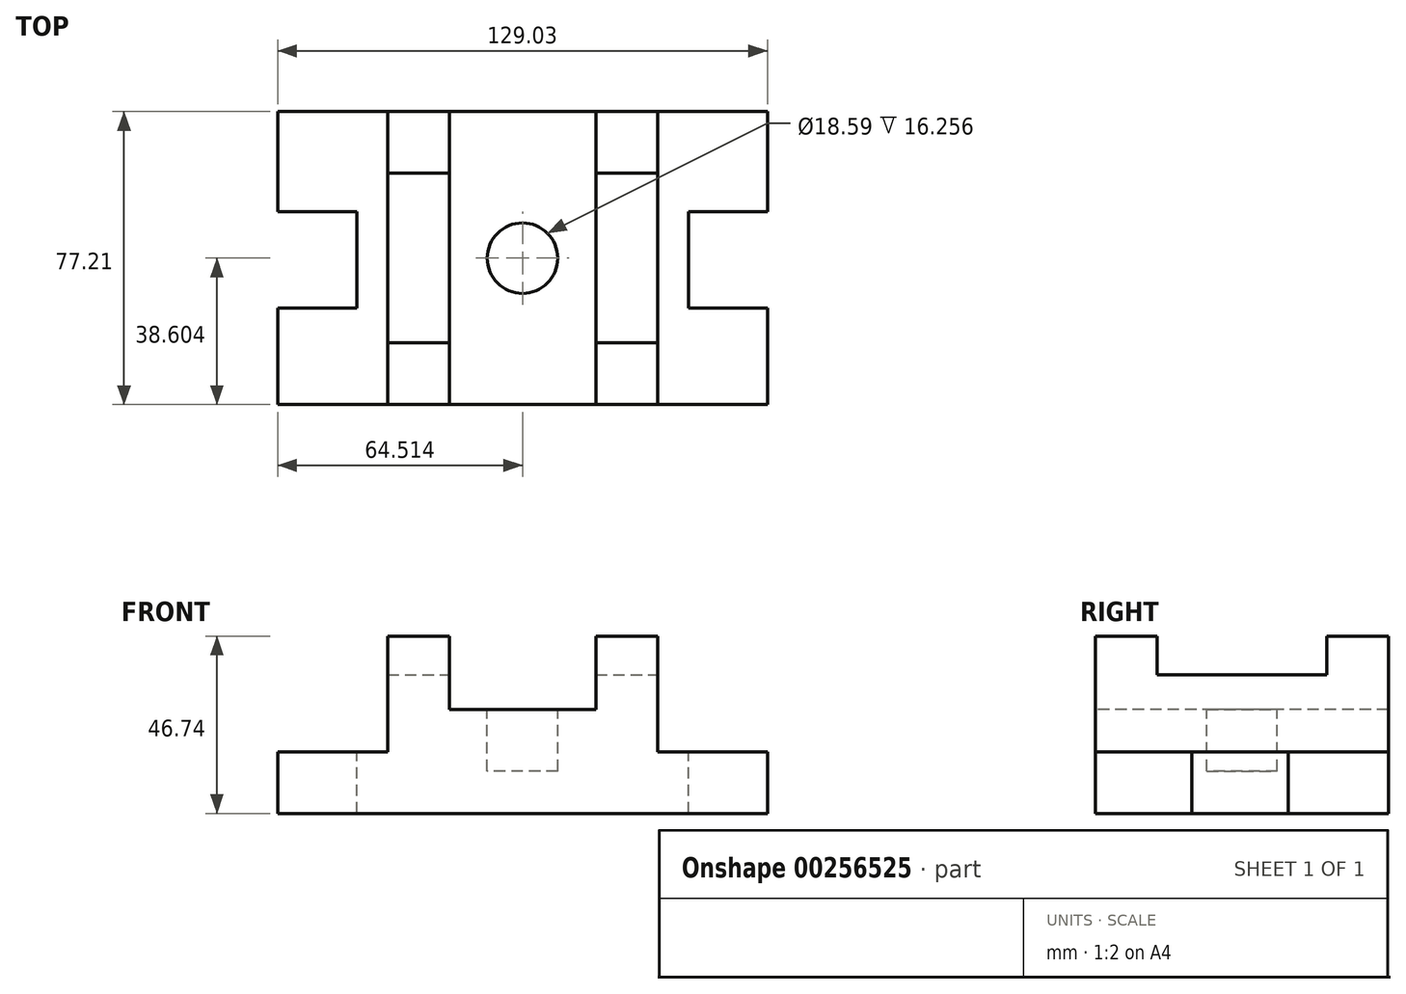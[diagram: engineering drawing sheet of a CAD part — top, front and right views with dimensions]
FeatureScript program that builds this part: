
annotation { "Feature Type Name" : "Feature", "Feature Type Description" : "" }
export const myFeature = defineFeature(function(context is Context, id is Id, definition is map)
    precondition{}
    {
        {
            var Q0;
            Q0=qCreatedBy(makeId("Top.planeOp"),FACE);
            var sketch = newSketch(context, id + "F0", { "sketchPlane" : qUnion([Q0])});
            skLineSegment(sketch, "E0.bottom", {"start": v(-63.44, 39.07) * mm, "end": v(65.59, 39.07) * mm});
            skLineSegment(sketch, "E0.top", {"start": v(-63.44, -38.14) * mm, "end": v(65.59, -38.14) * mm});
            skLineSegment(sketch, "E0.left", {"start": v(-63.44, 39.07) * mm, "end": v(-63.44, -38.14) * mm});
            skLineSegment(sketch, "E0.right", {"start": v(65.59, 39.07) * mm, "end": v(65.59, -38.14) * mm});
            skSolve(sketch);
        }
        {
            var Q0;
            Q0 = qSketchRegion(id + "F0", true);
            extrude(context, id + "F1", {"entities" : qUnion([Q0]), "depth" : 46.74 * mm});
        }
        {
            var Q0;
            Q0=makeQuery(id+"F1.opExtrude","CAP_FACE",FACE,{"disambiguationData":[OSD([sQuery(id+"F0.wireOp",EDGE,"E0.bottom"),sQuery(id+"F0.wireOp",EDGE,"E0.top"),sQuery(id+"F0.wireOp",EDGE,"E0.left"),sQuery(id+"F0.wireOp",EDGE,"E0.right")])],"isStart":false});
            var sketch = newSketch(context, id + "F2", { "sketchPlane" : qUnion([Q0])});
            skLineSegment(sketch, "E1.bottom", {"start": v(-63.44, 39.07) * mm, "end": v(-34.49, 39.07) * mm});
            skLineSegment(sketch, "E1.top", {"start": v(-63.44, -38.14) * mm, "end": v(-34.49, -38.14) * mm});
            skLineSegment(sketch, "E1.left", {"start": v(-63.44, 39.07) * mm, "end": v(-63.44, -38.14) * mm});
            skLineSegment(sketch, "E1.right", {"start": v(-34.49, 39.07) * mm, "end": v(-34.49, -38.14) * mm});
            skLineSegment(sketch, "E2.bottom", {"start": v(65.59, 39.07) * mm, "end": v(36.63, 39.07) * mm});
            skLineSegment(sketch, "E2.top", {"start": v(65.59, -38.14) * mm, "end": v(36.63, -38.14) * mm});
            skLineSegment(sketch, "E2.left", {"start": v(65.59, 39.07) * mm, "end": v(65.59, -38.14) * mm});
            skLineSegment(sketch, "E2.right", {"start": v(36.63, 39.07) * mm, "end": v(36.63, -38.14) * mm});
            skSolve(sketch);
        }
        {
            var Q0;
            Q0=makeQuery(id+"F2.imprint","IMPRINT",FACE,{"disambiguationData":[TD([[makeQuery(id+"F2.imprint","IMPRINT",EDGE,{"derivedFrom":sQuery(id+"F2.wireOp",EDGE,"E1.bottom")}),-1.0]])]});
            extrude(context, id + "F3", {"entities" : qUnion([Q0]), "operationType" : NewBodyOperationType.REMOVE, "oppositeDirection" : true, "depth" : 30.48 * mm});
        }
        {
            var Q0;
            Q0=makeQuery(id+"F2.imprint","IMPRINT",FACE,{"disambiguationData":[TD([[makeQuery(id+"F2.imprint","IMPRINT",EDGE,{"derivedFrom":sQuery(id+"F2.wireOp",EDGE,"E2.bottom")}),-1.0]])]});
            extrude(context, id + "F4", {"entities" : qUnion([Q0]), "operationType" : NewBodyOperationType.REMOVE, "oppositeDirection" : true, "depth" : 30.48 * mm});
        }
        {
            var Q0;
            Q0=makeQuery(id+"F1.opExtrude","CAP_FACE",FACE,{"disambiguationData":[OSD([sQuery(id+"F0.wireOp",EDGE,"E0.bottom"),sQuery(id+"F0.wireOp",EDGE,"E0.top"),sQuery(id+"F0.wireOp",EDGE,"E0.left"),sQuery(id+"F0.wireOp",EDGE,"E0.right")])],"isStart":false});
            var sketch = newSketch(context, id + "F5", { "sketchPlane" : qUnion([Q0])});
            skLineSegment(sketch, "E3", {"start": v(-34.49, 39.07) * mm, "end": v(-18.23, 39.07) * mm});
            skLineSegment(sketch, "E4", {"start": v(36.63, 39.07) * mm, "end": v(20.38, 39.07) * mm});
            skLineSegment(sketch, "E5.bottom", {"start": v(-18.23, 39.07) * mm, "end": v(20.38, 39.07) * mm});
            skLineSegment(sketch, "E5.top", {"start": v(-18.23, -38.14) * mm, "end": v(20.38, -38.14) * mm});
            skLineSegment(sketch, "E5.left", {"start": v(-18.23, 39.07) * mm, "end": v(-18.23, -38.14) * mm});
            skLineSegment(sketch, "E5.right", {"start": v(20.38, 39.07) * mm, "end": v(20.38, -38.14) * mm});
            skSolve(sketch);
        }
        {
            var Q0;
            Q0=makeQuery(id+"F5.imprint","IMPRINT",FACE,{"disambiguationData":[TD([[makeQuery(id+"F5.imprint","IMPRINT",EDGE,{"derivedFrom":sQuery(id+"F5.wireOp",EDGE,"E5.bottom")}),-1.0]])]});
            extrude(context, id + "F6", {"entities" : qUnion([Q0]), "operationType" : NewBodyOperationType.REMOVE, "oppositeDirection" : true, "depth" : 19.3 * mm});
        }
        {
            var Q0;
            {var subQ0=sQuery(id+"F0.wireOp",EDGE,"E0.bottom");var subQ1=sQuery(id+"F0.wireOp",EDGE,"E0.top");Q0=makeQuery(id+"F6.boolean.opBoolean","SPLIT",FACE,{"disambiguationData":[TD([makeQuery(id+"F3.boolean.opBoolean","COPY",FACE,{"derivedFrom":makeQuery(id+"F3.opExtrude","SWEPT_FACE",FACE,{"disambiguationData":[OSD([sQuery(id+"F2.wireOp",EDGE,"E1.right")])]})})])],"derivedFrom":makeQuery(id+"F1.opExtrude","CAP_FACE",FACE,{"disambiguationData":[OSD([subQ0,subQ1,sQuery(id+"F0.wireOp",EDGE,"E0.left"),sQuery(id+"F0.wireOp",EDGE,"E0.right")])],"isStart":false})});}
            var sketch = newSketch(context, id + "F7", { "sketchPlane" : qUnion([Q0])});
            skLineSegment(sketch, "E6", {"start": v(-34.49, 39.07) * mm, "end": v(-34.49, 22.82) * mm});
            skLineSegment(sketch, "E7.bottom", {"start": v(-34.49, 22.82) * mm, "end": v(-18.23, 22.82) * mm});
            skLineSegment(sketch, "E7.top", {"start": v(-34.49, -21.89) * mm, "end": v(-18.23, -21.89) * mm});
            skLineSegment(sketch, "E7.left", {"start": v(-34.49, 22.82) * mm, "end": v(-34.49, -21.89) * mm});
            skLineSegment(sketch, "E7.right", {"start": v(-18.23, 22.82) * mm, "end": v(-18.23, -21.89) * mm});
            skSolve(sketch);
        }
        {
            var Q0;
            Q0=makeQuery(id+"F7.imprint","IMPRINT",FACE,{"disambiguationData":[TD([[makeQuery(id+"F7.imprint","IMPRINT",EDGE,{"derivedFrom":sQuery(id+"F7.wireOp",EDGE,"E7.bottom")}),-1.0]])]});
            extrude(context, id + "F8", {"entities" : qUnion([Q0]), "operationType" : NewBodyOperationType.REMOVE, "oppositeDirection" : true, "depth" : 10.16 * mm});
        }
        {
            var Q0;
            {var subQ0=sQuery(id+"F0.wireOp",EDGE,"E0.bottom");var subQ1=sQuery(id+"F0.wireOp",EDGE,"E0.top");Q0=makeQuery(id+"F6.boolean.opBoolean","SPLIT",FACE,{"disambiguationData":[TD([makeQuery(id+"F4.boolean.opBoolean","COPY",FACE,{"derivedFrom":makeQuery(id+"F4.opExtrude","SWEPT_FACE",FACE,{"disambiguationData":[OSD([sQuery(id+"F2.wireOp",EDGE,"E2.right")])]})})])],"derivedFrom":makeQuery(id+"F1.opExtrude","CAP_FACE",FACE,{"disambiguationData":[OSD([subQ0,subQ1,sQuery(id+"F0.wireOp",EDGE,"E0.left"),sQuery(id+"F0.wireOp",EDGE,"E0.right")])],"isStart":false})});}
            var sketch = newSketch(context, id + "F9", { "sketchPlane" : qUnion([Q0])});
            skLineSegment(sketch, "E8", {"start": v(20.38, 39.07) * mm, "end": v(20.38, 22.82) * mm});
            skLineSegment(sketch, "E9.bottom", {"start": v(20.38, 22.82) * mm, "end": v(36.63, 22.82) * mm});
            skLineSegment(sketch, "E9.top", {"start": v(20.38, -21.89) * mm, "end": v(36.63, -21.89) * mm});
            skLineSegment(sketch, "E9.left", {"start": v(20.38, 22.82) * mm, "end": v(20.38, -21.89) * mm});
            skLineSegment(sketch, "E9.right", {"start": v(36.63, 22.82) * mm, "end": v(36.63, -21.89) * mm});
            skSolve(sketch);
        }
        {
            var Q0;
            Q0=makeQuery(id+"F9.imprint","IMPRINT",FACE,{"disambiguationData":[TD([[makeQuery(id+"F9.imprint","IMPRINT",EDGE,{"derivedFrom":sQuery(id+"F9.wireOp",EDGE,"E9.bottom")}),-1.0]])]});
            extrude(context, id + "F10", {"entities" : qUnion([Q0]), "operationType" : NewBodyOperationType.REMOVE, "oppositeDirection" : true, "depth" : 10.16 * mm});
        }
        {
            var Q0;
            Q0=makeQuery(id+"F4.boolean.opBoolean","COPY",FACE,{"derivedFrom":makeQuery(id+"F4.opExtrude","CAP_FACE",FACE,{"disambiguationData":[OSD([sQuery(id+"F2.wireOp",EDGE,"E2.bottom"),sQuery(id+"F2.wireOp",EDGE,"E2.top"),sQuery(id+"F2.wireOp",EDGE,"E2.left"),sQuery(id+"F2.wireOp",EDGE,"E2.right")])],"isStart":false})});
            var sketch = newSketch(context, id + "F11", { "sketchPlane" : qUnion([Q0])});
            skLineSegment(sketch, "E10", {"start": v(65.59, 39.07) * mm, "end": v(65.59, 12.66) * mm});
            skLineSegment(sketch, "E11.bottom", {"start": v(65.59, 12.66) * mm, "end": v(36.63, 12.66) * mm});
            skLineSegment(sketch, "E11.top", {"start": v(65.59, -12.74) * mm, "end": v(36.63, -12.74) * mm});
            skLineSegment(sketch, "E11.left", {"start": v(65.59, 12.66) * mm, "end": v(65.59, -12.74) * mm});
            skLineSegment(sketch, "E11.right", {"start": v(36.63, 12.66) * mm, "end": v(36.63, -12.74) * mm});
            skLineSegment(sketch, "E12", {"start": v(44.76, 12.66) * mm, "end": v(65.59, 12.66) * mm});
            skLineSegment(sketch, "E13", {"start": v(44.76, 12.66) * mm, "end": v(44.76, -12.74) * mm});
            skLineSegment(sketch, "E14", {"start": v(44.76, -12.74) * mm, "end": v(65.59, -12.74) * mm});
            skLineSegment(sketch, "E15", {"start": v(65.59, 12.66) * mm, "end": v(44.76, 12.66) * mm});
            skSolve(sketch);
        }
        {
            var Q0;
            Q0=makeQuery(id+"F11.imprint","IMPRINT",FACE,{"disambiguationData":[TD([[makeQuery(id+"F11.imprint","IMPRINT",EDGE,{"derivedFrom":sQuery(id+"F11.wireOp",EDGE,"E11.left")}),-1.0]])]});
            extrude(context, id + "F12", {"entities" : qUnion([Q0]), "operationType" : NewBodyOperationType.REMOVE, "oppositeDirection" : true, "depth" : 16.26 * mm});
        }
        {
            var Q0;
            Q0=makeQuery(id+"F3.boolean.opBoolean","COPY",FACE,{"derivedFrom":makeQuery(id+"F3.opExtrude","CAP_FACE",FACE,{"disambiguationData":[OSD([sQuery(id+"F2.wireOp",EDGE,"E1.bottom"),sQuery(id+"F2.wireOp",EDGE,"E1.top"),sQuery(id+"F2.wireOp",EDGE,"E1.left"),sQuery(id+"F2.wireOp",EDGE,"E1.right")])],"isStart":false})});
            var sketch = newSketch(context, id + "F13", { "sketchPlane" : qUnion([Q0])});
            skLineSegment(sketch, "E16", {"start": v(-63.44, 39.07) * mm, "end": v(-63.44, 12.66) * mm});
            skLineSegment(sketch, "E17.bottom", {"start": v(-63.44, 12.66) * mm, "end": v(-42.61, 12.66) * mm});
            skLineSegment(sketch, "E17.top", {"start": v(-63.44, -12.74) * mm, "end": v(-42.61, -12.74) * mm});
            skLineSegment(sketch, "E17.left", {"start": v(-63.44, 12.66) * mm, "end": v(-63.44, -12.74) * mm});
            skLineSegment(sketch, "E17.right", {"start": v(-42.61, 12.66) * mm, "end": v(-42.61, -12.74) * mm});
            skSolve(sketch);
        }
        {
            var Q0;
            Q0=makeQuery(id+"F13.imprint","IMPRINT",FACE,{"disambiguationData":[TD([[makeQuery(id+"F13.imprint","IMPRINT",EDGE,{"derivedFrom":sQuery(id+"F13.wireOp",EDGE,"E17.bottom")}),-1.0]])]});
            extrude(context, id + "F14", {"entities" : qUnion([Q0]), "operationType" : NewBodyOperationType.REMOVE, "oppositeDirection" : true, "depth" : 16.26 * mm});
        }
        {
            var Q0;
            Q0=makeQuery(id+"F6.boolean.opBoolean","COPY",FACE,{"derivedFrom":makeQuery(id+"F6.opExtrude","CAP_FACE",FACE,{"disambiguationData":[OSD([sQuery(id+"F5.wireOp",EDGE,"E5.bottom"),sQuery(id+"F5.wireOp",EDGE,"E5.top"),sQuery(id+"F5.wireOp",EDGE,"E5.left"),sQuery(id+"F5.wireOp",EDGE,"E5.right")])],"isStart":false})});
            var sketch = newSketch(context, id + "F15", { "sketchPlane" : qUnion([Q0])});
            skPoint(sketch, "E18.startSnap0", {"position": v(1.07, 39.07) * mm});
            skLineSegment(sketch, "E19", {"start": v(1.07, 39.07) * mm, "end": v(65.59, 39.07) * mm});
            skLineSegment(sketch, "E20", {"start": v(13.26, -38.14) * mm, "end": v(13.26, 0.46) * mm});
            skCircle(sketch, "E21", {"center": v(1.07, 0.46) * mm, "radius": 9.3 * mm});
            skSolve(sketch);
        }
        {
            var Q0;
            Q0=makeQuery(id+"F15.imprint","IMPRINT",FACE,{"disambiguationData":[TD([[makeQuery(id+"F15.imprint","IMPRINT",EDGE,{"derivedFrom":sQuery(id+"F15.wireOp",EDGE,"E21")}),1.0]])]});
            extrude(context, id + "F16", {"entities" : qUnion([Q0]), "operationType" : NewBodyOperationType.REMOVE, "oppositeDirection" : true, "depth" : 16.26 * mm});
        }
    });
